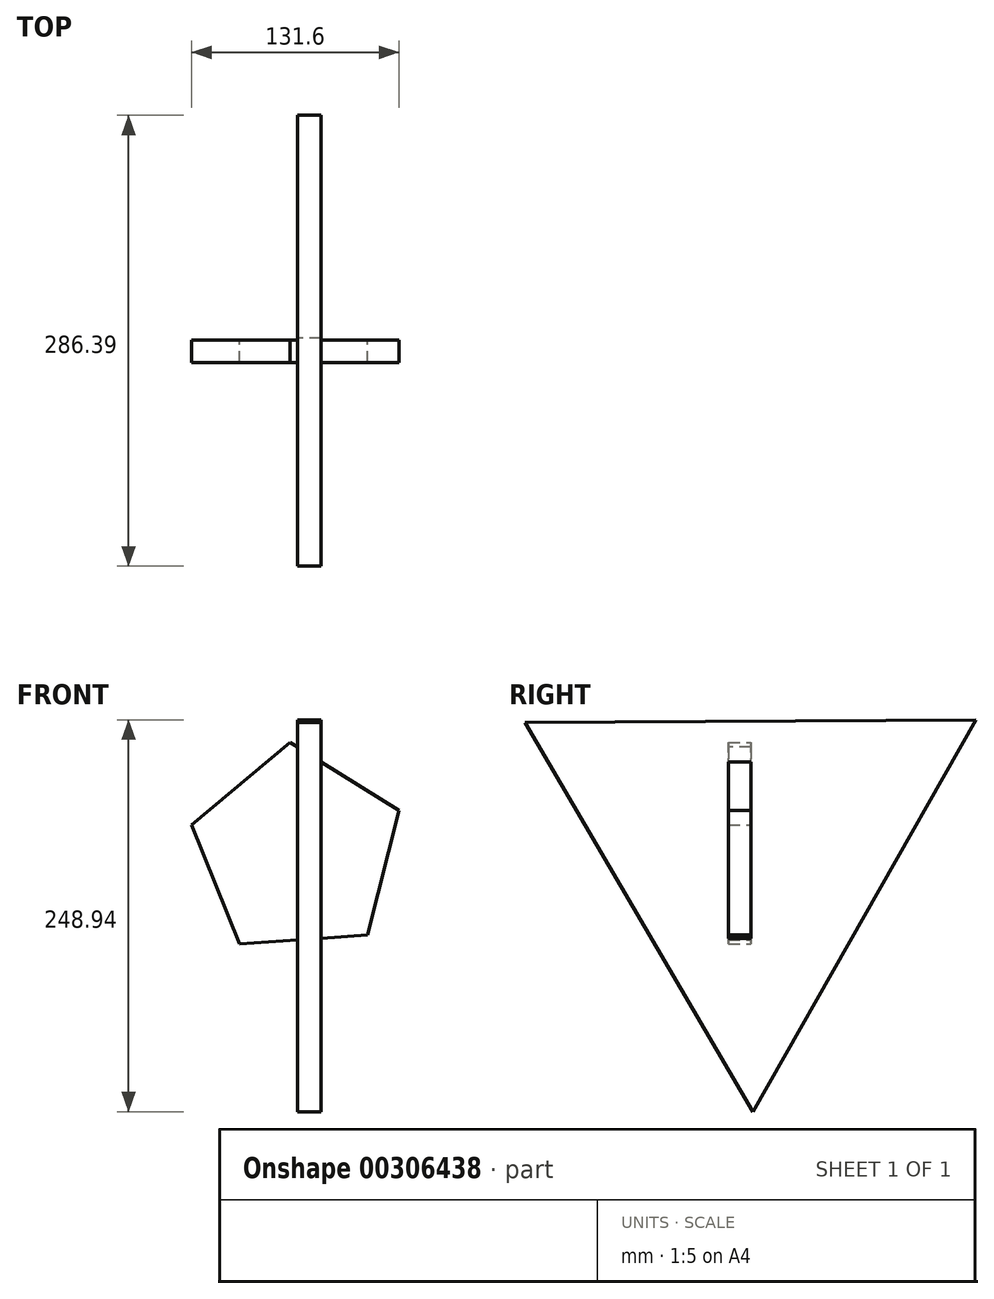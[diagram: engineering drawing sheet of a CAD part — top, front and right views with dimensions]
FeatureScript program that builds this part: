
annotation { "Feature Type Name" : "Feature", "Feature Type Description" : "" }
export const myFeature = defineFeature(function(context is Context, id is Id, definition is map)
    precondition{}
    {
        {
            var Q0;
            Q0=qCreatedBy(makeId("Front.planeOp"),FACE);
            var sketch = newSketch(context, id + "F0", { "sketchPlane" : qUnion([Q0])});
            skCircle(sketch, "E0.cCircle", {"center": v(0, 0) * mm, "radius": 56.1 * mm, "construction": true});
            skLineSegment(sketch, "E0.0", {"start": v(64.35, 25.84) * mm, "end": v(44.46, -53.22) * mm});
            skLineSegment(sketch, "E0.1", {"start": v(44.46, -53.22) * mm, "end": v(-36.87, -58.73) * mm});
            skLineSegment(sketch, "E0.2", {"start": v(-36.87, -58.73) * mm, "end": v(-67.25, 16.92) * mm});
            skLineSegment(sketch, "E0.3", {"start": v(-67.25, 16.92) * mm, "end": v(-4.69, 69.18) * mm});
            skLineSegment(sketch, "E0.4", {"start": v(-4.69, 69.18) * mm, "end": v(64.35, 25.84) * mm});
            skPoint(sketch, "E0.0.midPoint", {"position": v(54.4, -13.7) * mm});
            skSolve(sketch);
        }
        {
            var Q0;
            Q0=qCreatedBy(makeId("Right.planeOp"),FACE);
            var sketch = newSketch(context, id + "F1", { "sketchPlane" : qUnion([Q0])});
            skCircle(sketch, "E1.cCircle", {"center": v(0, 0) * mm, "radius": 82.68 * mm, "construction": true});
            skLineSegment(sketch, "E1.0", {"start": v(1.05, -165.35) * mm, "end": v(-143.72, 81.77) * mm});
            skLineSegment(sketch, "E1.1", {"start": v(-143.72, 81.77) * mm, "end": v(142.67, 83.59) * mm});
            skLineSegment(sketch, "E1.2", {"start": v(142.67, 83.59) * mm, "end": v(1.05, -165.35) * mm});
            skPoint(sketch, "E1.0.midPoint", {"position": v(-71.34, -41.8) * mm});
            skSolve(sketch);
        }
        {
            var Q0;
            Q0=makeQuery(id+"F1.imprint","IMPRINT",FACE,{"disambiguationData":[TD([[makeQuery(id+"F1.imprint","IMPRINT",EDGE,{"derivedFrom":sQuery(id+"F1.wireOp",EDGE,"E1.0")}),-1.0]])]});
            extrude(context, id + "F2", {"entities" : qUnion([Q0]), "depth" : 15 * mm});
        }
        {
            var Q0;
            Q0=makeQuery(id+"F0.imprint","IMPRINT",FACE,{"disambiguationData":[TD([[makeQuery(id+"F0.imprint","IMPRINT",EDGE,{"derivedFrom":sQuery(id+"F0.wireOp",EDGE,"E0.0")}),-1.0]])]});
            extrude(context, id + "F3", {"entities" : qUnion([Q0]), "operationType" : NewBodyOperationType.ADD, "depth" : 14.48 * mm});
        }
    });
